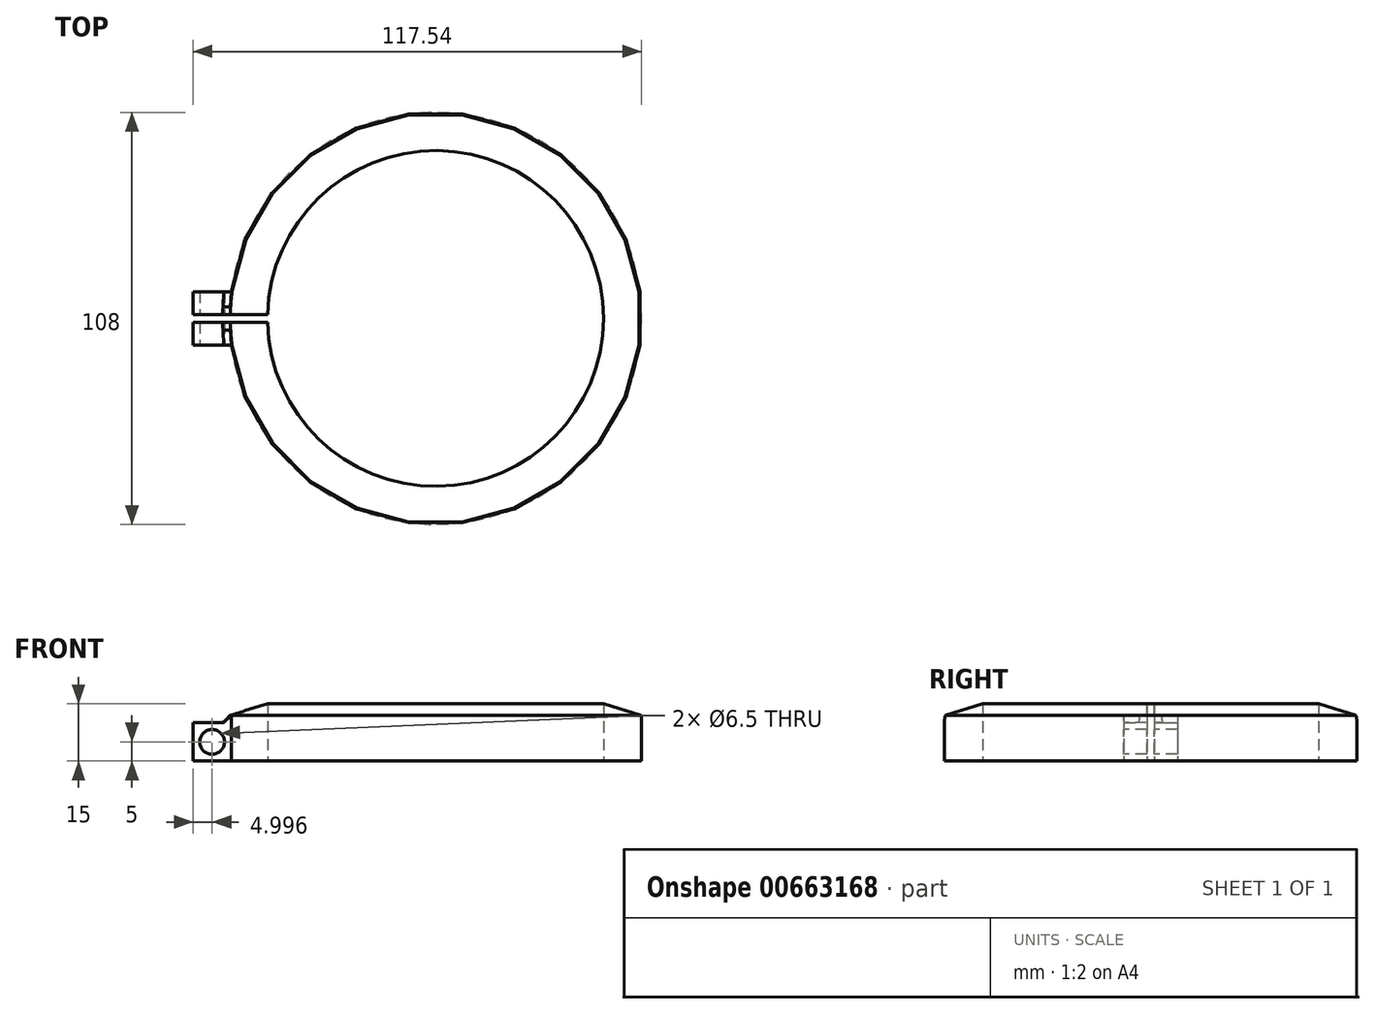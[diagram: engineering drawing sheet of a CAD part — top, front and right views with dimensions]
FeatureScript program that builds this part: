
annotation { "Feature Type Name" : "Feature", "Feature Type Description" : "" }
export const myFeature = defineFeature(function(context is Context, id is Id, definition is map)
    precondition{}
    {
        {
            var Q0;
            Q0=qCreatedBy(makeId("Top.planeOp"),FACE);
            var sketch = newSketch(context, id + "F0", { "sketchPlane" : qUnion([Q0])});
            skCircle(sketch, "E0", {"center": v(0, 0) * mm, "radius": 44 * mm, "construction": true});
            skCircle(sketch, "E1", {"center": v(0, 0) * mm, "radius": 54 * mm, "construction": true});
            skLineSegment(sketch, "E2", {"start": v(0, 0) * mm, "end": v(-54, 0) * mm, "construction": true});
            skPoint(sketch, "E3", {"position": v(-44, 0) * mm});
            skPoint(sketch, "E4", {"position": v(-43.99, 1) * mm});
            skPoint(sketch, "E5", {"position": v(-43.99, -1) * mm});
            skLineSegment(sketch, "E6", {"start": v(-43.99, 1) * mm, "end": v(-63.54, 1) * mm});
            skLineSegment(sketch, "E7", {"start": v(-63.54, 1) * mm, "end": v(-63.54, 7) * mm});
            skLineSegment(sketch, "E8", {"start": v(-63.54, 7) * mm, "end": v(-53.54, 7) * mm});
            skLineSegment(sketch, "E9", {"start": v(-43.99, -1) * mm, "end": v(-63.54, -1) * mm});
            skLineSegment(sketch, "E10", {"start": v(-63.54, -1) * mm, "end": v(-63.54, -7) * mm});
            skLineSegment(sketch, "E11", {"start": v(-63.54, -7) * mm, "end": v(-53.54, -7) * mm});
            skArc(sketch, "E12", {"start": v(-43.99, -1) * mm, "mid": v(44, 0) * mm, "end": v(-43.99, 1) * mm});
            skArc(sketch, "E13", {"start": v(-53.54, -7) * mm, "mid": v(54, 0) * mm, "end": v(-53.54, 7) * mm});
            skSolve(sketch);
        }
        {
            var Q0;
            Q0 = qSketchRegion(id + "F0", true);
            extrude(context, id + "F1", {"entities" : qUnion([Q0]), "depth" : 12 * mm, "offsetDistance" : 25 * mm});
        }
        {
            var Q0;
            Q0=makeQuery(id+"F1.opExtrude","SWEPT_FACE",FACE,{"disambiguationData":[OSD([sQuery(id+"F0.wireOp",EDGE,"E6")])]});
            var sketch = newSketch(context, id + "F2", { "sketchPlane" : qUnion([Q0])});
            skLineSegment(sketch, "E14", {"start": v(-43.99, 12) * mm, "end": v(-53.77, 12) * mm});
            skLineSegment(sketch, "E15", {"start": v(-53.77, 12) * mm, "end": v(-43.99, 15) * mm});
            skLineSegment(sketch, "E16", {"start": v(-43.99, 15) * mm, "end": v(-43.99, 12) * mm});
            skSolve(sketch);
        }
        {
            var Q0;
            Q0 = qSketchRegion(id + "F2", true);
            var Q1;
            Q1=makeQuery(id+"F1.opExtrude","SWEPT_FACE",FACE,{"disambiguationData":[OSD([sQuery(id+"F0.wireOp",EDGE,"E12")])]});
            revolve(context, id + "F3", {"operationType" : NewBodyOperationType.ADD, "surfaceOperationType" : NewSurfaceOperationType.NEW, "entities" : qUnion([Q0]), "axis" : qUnion([Q1]), "revolveType" : RevolveType.FULL});
        }
        {
            var Q0;
            Q0=makeQuery(id+"F3.opRevolve","SWEPT_FACE",FACE,{"disambiguationData":[OSD([sQuery(id+"F2.wireOp",EDGE,"E14")])]});
            var sketch = newSketch(context, id + "F4", { "sketchPlane" : qUnion([Q0])});
            skLineSegment(sketch, "E17.bottom", {"start": v(-53.77, 1) * mm, "end": v(-43.99, 1) * mm});
            skLineSegment(sketch, "E17.top", {"start": v(-53.77, -1) * mm, "end": v(-43.99, -1) * mm});
            skLineSegment(sketch, "E17.left", {"start": v(-53.77, 1) * mm, "end": v(-53.77, -1) * mm});
            skLineSegment(sketch, "E17.right", {"start": v(-43.99, 1) * mm, "end": v(-43.99, -1) * mm});
            skSolve(sketch);
        }
        {
            var Q0;
            Q0 = qSketchRegion(id + "F4", true);
            extrude(context, id + "F5", {"entities" : qUnion([Q0]), "operationType" : NewBodyOperationType.REMOVE, "oppositeDirection" : true, "depth" : 25 * mm, "offsetDistance" : 25 * mm});
        }
        {
            var Q0;
            Q0=makeQuery(id+"F1.opExtrude","CAP_FACE",FACE,{"disambiguationData":[OSD([sQuery(id+"F0.wireOp",EDGE,"E6"),sQuery(id+"F0.wireOp",EDGE,"E7"),sQuery(id+"F0.wireOp",EDGE,"E8"),sQuery(id+"F0.wireOp",EDGE,"E9"),sQuery(id+"F0.wireOp",EDGE,"E10"),sQuery(id+"F0.wireOp",EDGE,"E11"),sQuery(id+"F0.wireOp",EDGE,"E12"),sQuery(id+"F0.wireOp",EDGE,"E13")])],"isStart":false});
            var sketch = newSketch(context, id + "F6", { "sketchPlane" : qUnion([Q0])});
            skLineSegment(sketch, "E18", {"start": v(-53.54, 7) * mm, "end": v(-53.77, 1) * mm});
            skLineSegment(sketch, "E19", {"start": v(-53.77, 1) * mm, "end": v(-63.54, 1) * mm});
            skLineSegment(sketch, "E20", {"start": v(-63.54, 1) * mm, "end": v(-63.54, 7) * mm});
            skLineSegment(sketch, "E21", {"start": v(-63.54, 7) * mm, "end": v(-53.54, 7) * mm});
            skLineSegment(sketch, "E22", {"start": v(-53.54, -7) * mm, "end": v(-53.77, -1) * mm});
            skLineSegment(sketch, "E23", {"start": v(-53.77, -1) * mm, "end": v(-63.54, -1) * mm});
            skLineSegment(sketch, "E24", {"start": v(-63.54, -1) * mm, "end": v(-63.54, -7) * mm});
            skLineSegment(sketch, "E25", {"start": v(-63.54, -7) * mm, "end": v(-53.54, -7) * mm});
            skSolve(sketch);
        }
        {
            var Q0;
            Q0 = qSketchRegion(id + "F6", true);
            extrude(context, id + "F7", {"entities" : qUnion([Q0]), "operationType" : NewBodyOperationType.REMOVE, "oppositeDirection" : true, "depth" : 2 * mm, "offsetDistance" : 25 * mm});
        }
        {
            var Q0;
            Q0=makeQuery(id+"F7.boolean.opBoolean","COPY",EDGE,{"derivedFrom":makeQuery(id+"F7.opExtrude","CAP_EDGE",EDGE,{"disambiguationData":[OSD([sQuery(id+"F6.wireOp",EDGE,"E18")])],"isStart":false})});
            chamfer(context, id + "F8", {"entities" : qUnion([Q0]), "width" : 2 * mm, "tangentPropagation" : true});
        }
        {
            var Q0;
            Q0=makeQuery(id+"F7.boolean.opBoolean","COPY",EDGE,{"derivedFrom":makeQuery(id+"F7.opExtrude","CAP_EDGE",EDGE,{"disambiguationData":[OSD([sQuery(id+"F6.wireOp",EDGE,"E22")])],"isStart":false})});
            chamfer(context, id + "F9", {"entities" : qUnion([Q0]), "width" : 2 * mm, "tangentPropagation" : true});
        }
        {
            var Q0;
            Q0=makeQuery(id+"F1.opExtrude","CAP_EDGE",EDGE,{"disambiguationData":[OSD([sQuery(id+"F0.wireOp",EDGE,"E13")])],"isStart":false});
            fillet(context, id + "F10", {"entities" : qUnion([Q0]), "radius" : 5 * mm, "tangentPropagation" : true, "allowEdgeOverflow" : false});
        }
        {
            var Q0;
            Q0=makeQuery(id+"F1.opExtrude","SWEPT_FACE",FACE,{"disambiguationData":[OSD([sQuery(id+"F0.wireOp",EDGE,"E11")])]});
            var sketch = newSketch(context, id + "F11", { "sketchPlane" : qUnion([Q0])});
            skLineSegment(sketch, "E26", {"start": v(-63.54, 5) * mm, "end": v(-53.54, 5) * mm, "construction": true});
            skLineSegment(sketch, "E27", {"start": v(-58.54, 0) * mm, "end": v(-58.54, 5) * mm, "construction": true});
            skCircle(sketch, "E28", {"center": v(-58.54, 5) * mm, "radius": 3.25 * mm});
            skSolve(sketch);
        }
        {
            var Q0;
            Q0 = qSketchRegion(id + "F11", true);
            extrude(context, id + "F12", {"entities" : qUnion([Q0]), "operationType" : NewBodyOperationType.REMOVE, "oppositeDirection" : true, "depth" : 25 * mm, "offsetDistance" : 25 * mm});
        }
    });
